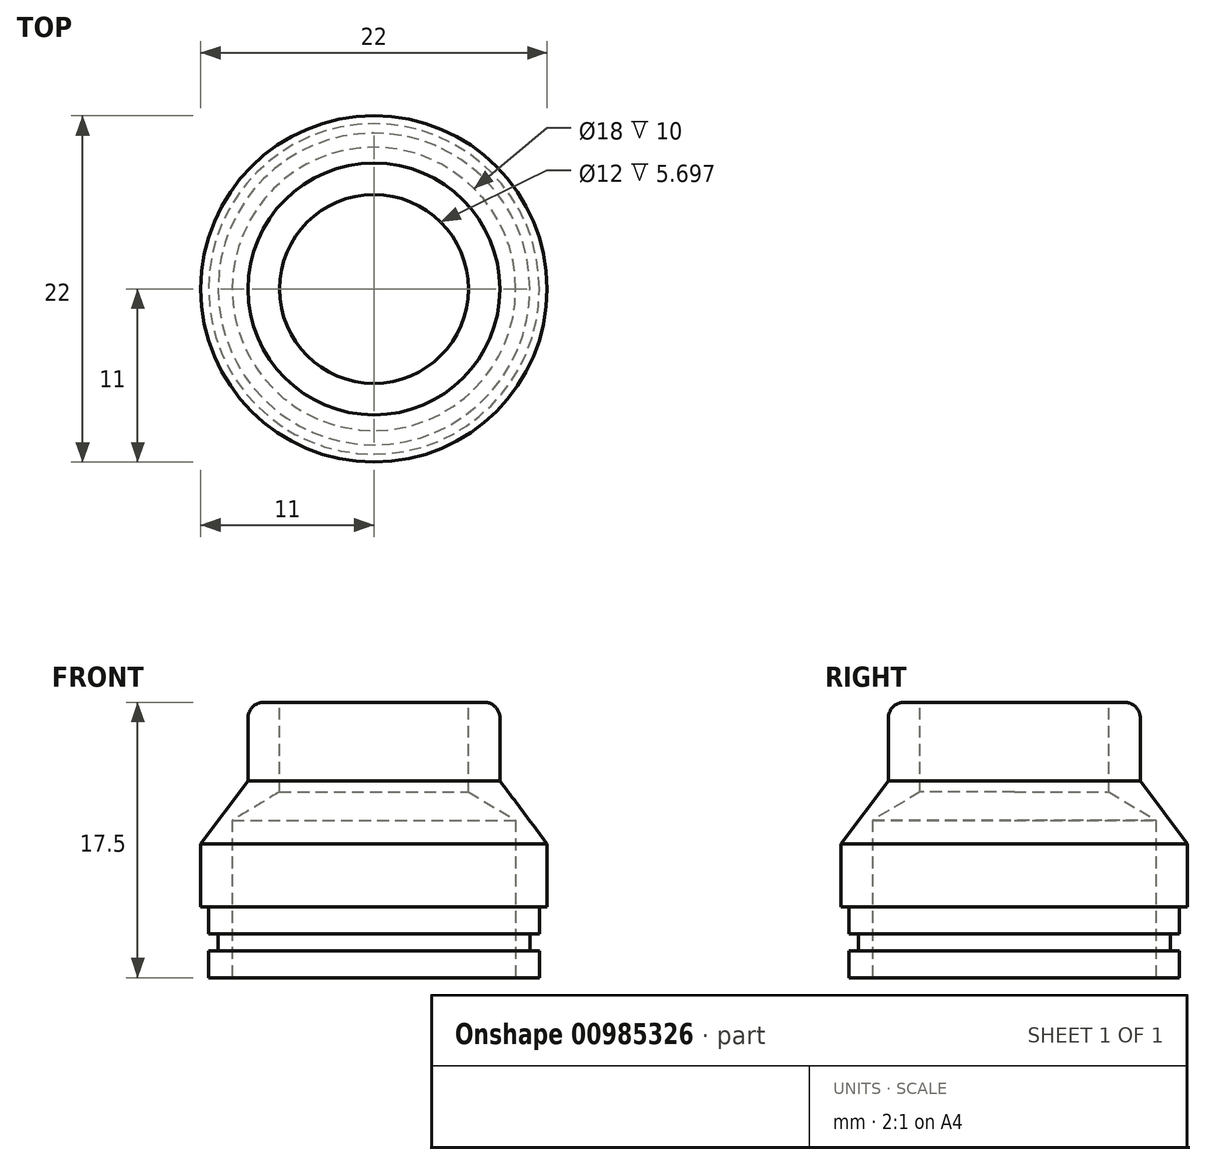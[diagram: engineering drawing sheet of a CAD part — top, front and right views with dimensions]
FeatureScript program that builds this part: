
annotation { "Feature Type Name" : "Feature", "Feature Type Description" : "" }
export const myFeature = defineFeature(function(context is Context, id is Id, definition is map)
    precondition{}
    {
        {
            var Q0;
            Q0=qCreatedBy(makeId("Top.planeOp"),FACE);
            var sketch = newSketch(context, id + "F0", { "sketchPlane" : qUnion([Q0])});
            skCircle(sketch, "E0", {"center": v(0, 0) * mm, "radius": 10.5 * mm});
            skCircle(sketch, "E1", {"center": v(0, 0) * mm, "radius": 9.9 * mm});
            skSolve(sketch);
        }
        {
            var Q0;
            Q0 = qSketchRegion(id + "F0", true);
            extrude(context, id + "F1", {"entities" : qUnion([Q0]), "depth" : 1.7 * mm, "offsetDistance" : 25 * mm});
        }
        {
            var Q0;
            Q0=makeQuery(id+"F0.imprint","IMPRINT",FACE,{"disambiguationData":[TD([[makeQuery(id+"F0.imprint","IMPRINT",EDGE,{"derivedFrom":sQuery(id+"F0.wireOp",EDGE,"E1")}),1.0]])]});
            extrude(context, id + "F2", {"entities" : qUnion([Q0]), "operationType" : NewBodyOperationType.ADD, "depth" : 2.8 * mm, "offsetDistance" : 25 * mm});
        }
        {
            var Q0;
            Q0=makeQuery(id+"F2.opExtrude","CAP_FACE",FACE,{"disambiguationData":[OSD([sQuery(id+"F0.wireOp",EDGE,"E1")])],"isStart":false});
            var sketch = newSketch(context, id + "F3", { "sketchPlane" : qUnion([Q0])});
            skCircle(sketch, "E2", {"center": v(0, 0) * mm, "radius": 10.5 * mm});
            skSolve(sketch);
        }
        {
            var Q0;
            Q0 = qSketchRegion(id + "F3", true);
            extrude(context, id + "F4", {"entities" : qUnion([Q0]), "operationType" : NewBodyOperationType.ADD, "depth" : 1.7 * mm, "offsetDistance" : 25 * mm});
        }
        {
            var Q0;
            Q0=makeQuery(id+"F4.opExtrude","CAP_FACE",FACE,{"disambiguationData":[OSD([sQuery(id+"F3.wireOp",EDGE,"E2")])],"isStart":false});
            var sketch = newSketch(context, id + "F5", { "sketchPlane" : qUnion([Q0])});
            skCircle(sketch, "E3", {"center": v(0, 0) * mm, "radius": 11 * mm});
            skSolve(sketch);
        }
        {
            var Q0;
            Q0 = qSketchRegion(id + "F5", true);
            extrude(context, id + "F6", {"entities" : qUnion([Q0]), "operationType" : NewBodyOperationType.ADD, "depth" : 8 * mm, "offsetDistance" : 25 * mm});
        }
        {
            var Q0;
            Q0=makeQuery(id+"F6.opExtrude","CAP_EDGE",EDGE,{"disambiguationData":[OSD([sQuery(id+"F5.wireOp",EDGE,"E3")])],"isStart":false});
            chamfer(context, id + "F7", {"entities" : qUnion([Q0]), "chamferType" : ChamferType.TWO_OFFSETS, "width1" : 3 * mm, "oppositeDirection" : false, "width2" : 4 * mm, "tangentPropagation" : true});
        }
        {
            var Q0;
            Q0=makeQuery(id+"F6.opExtrude","CAP_FACE",FACE,{"disambiguationData":[OSD([sQuery(id+"F5.wireOp",EDGE,"E3")])],"isStart":false});
            var sketch = newSketch(context, id + "F8", { "sketchPlane" : qUnion([Q0])});
            skCircle(sketch, "E4", {"center": v(0, 0) * mm, "radius": 8 * mm});
            skSolve(sketch);
        }
        {
            var Q0;
            Q0 = qSketchRegion(id + "F8", true);
            extrude(context, id + "F9", {"entities" : qUnion([Q0]), "operationType" : NewBodyOperationType.ADD, "depth" : 5 * mm, "offsetDistance" : 25 * mm});
        }
        {
            var Q0;
            {var subQ0=sQuery(id+"F0.wireOp",EDGE,"E1");Q0=makeQuery(id+"F2.boolean.opBoolean","MERGE",FACE,{"derivedFrom":[makeQuery(id+"F1.opExtrude","CAP_FACE",FACE,{"disambiguationData":[OSD([sQuery(id+"F0.wireOp",EDGE,"E0"),subQ0])],"isStart":true}),makeQuery(id+"F2.opExtrude","CAP_FACE",FACE,{"disambiguationData":[OSD([subQ0])],"isStart":true})]});}
            var sketch = newSketch(context, id + "F10", { "sketchPlane" : qUnion([Q0])});
            skPoint(sketch, "E5", {"position": v(0, 0) * mm});
            skSolve(sketch);
        }
        {
            var Q0;
            Q0=sQuery(id+"F10.wireOp",VERTEX,"E5");
            var Q1;
            Q1=makeQuery(id+"F1.opExtrude","SWEPT_BODY",BODY,{"disambiguationData":[OSD([sQuery(id+"F0.wireOp",EDGE,"E0"),sQuery(id+"F0.wireOp",EDGE,"E1")])]});
            hole(context, id + "F11", {"style" : HoleStyle.SIMPLE, "endStyle" : HoleEndStyle.BLIND, "holeDiameter" : 18 * mm, "majorDiameter" : 5 * mm, "holeDepth" : 10 * mm, "isTappedThrough" : true, "tappedDepth" : 12 * mm, "tapClearance" : 3, "locations" : qUnion([Q0]), "scope" : qUnion([Q1])});
        }
        {
            var Q0;
            Q0=makeQuery(id+"F9.opExtrude","CAP_FACE",FACE,{"disambiguationData":[OSD([sQuery(id+"F8.wireOp",EDGE,"E4")])],"isStart":false});
            var sketch = newSketch(context, id + "F12", { "sketchPlane" : qUnion([Q0])});
            skPoint(sketch, "E6", {"position": v(0, 0) * mm});
            skSolve(sketch);
        }
        {
            var Q0;
            Q0=sQuery(id+"F12.wireOp",VERTEX,"E6");
            var Q1;
            Q1=makeQuery(id+"F1.opExtrude","SWEPT_BODY",BODY,{"disambiguationData":[OSD([sQuery(id+"F0.wireOp",EDGE,"E0"),sQuery(id+"F0.wireOp",EDGE,"E1")])]});
            hole(context, id + "F13", {"style" : HoleStyle.SIMPLE, "endStyle" : HoleEndStyle.THROUGH, "holeDiameter" : 12 * mm, "majorDiameter" : 5 * mm, "isTappedThrough" : true, "tappedDepth" : 12 * mm, "tapClearance" : 3, "locations" : qUnion([Q0]), "scope" : qUnion([Q1])});
        }
        {
            var Q0;
            Q0=makeQuery(id+"F9.opExtrude","CAP_EDGE",EDGE,{"disambiguationData":[OSD([sQuery(id+"F8.wireOp",EDGE,"E4")])],"isStart":false});
            fillet(context, id + "F14", {"entities" : qUnion([Q0]), "radius" : 1 * mm, "tangentPropagation" : true, "allowEdgeOverflow" : false});
        }
    });
